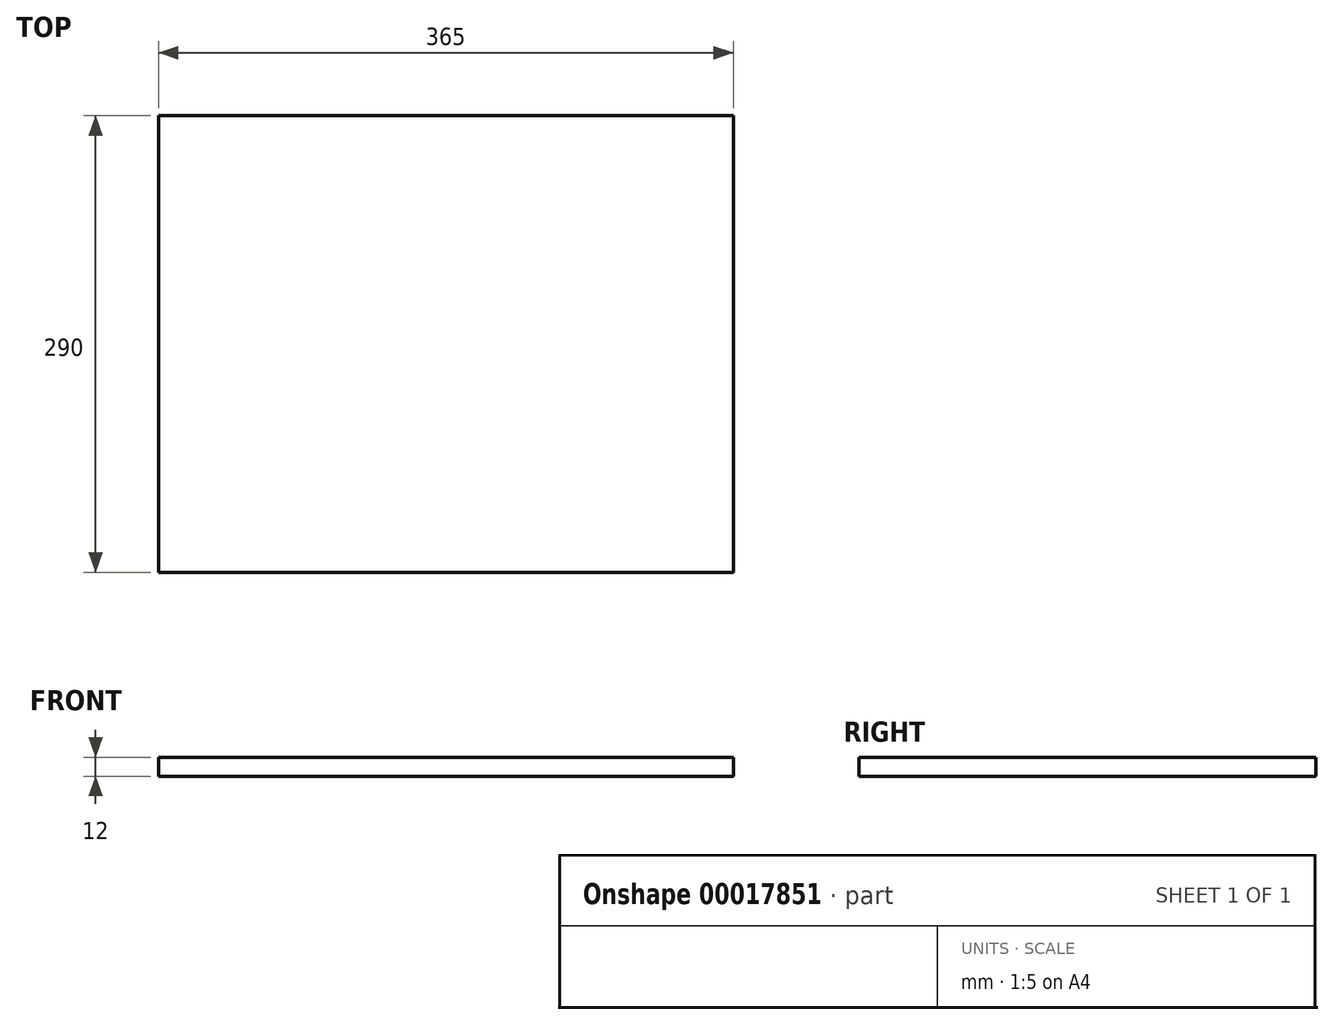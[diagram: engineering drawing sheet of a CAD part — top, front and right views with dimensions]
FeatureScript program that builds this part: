
annotation { "Feature Type Name" : "Feature", "Feature Type Description" : "" }
export const myFeature = defineFeature(function(context is Context, id is Id, definition is map)
    precondition{}
    {
        {
            var Q0;
            Q0=qCreatedBy(makeId("Top.planeOp"),FACE);
            var sketch = newSketch(context, id + "F0", { "sketchPlane" : qUnion([Q0])});
            skLineSegment(sketch, "E0.bottom", {"start": v(-70.96, 65.05) * mm, "end": v(294.04, 65.05) * mm});
            skLineSegment(sketch, "E0.top", {"start": v(-70.96, -224.95) * mm, "end": v(294.04, -224.95) * mm});
            skLineSegment(sketch, "E0.left", {"start": v(-70.96, 65.05) * mm, "end": v(-70.96, -224.95) * mm});
            skLineSegment(sketch, "E0.right", {"start": v(294.04, 65.05) * mm, "end": v(294.04, -224.95) * mm});
            skSolve(sketch);
        }
        {
            var Q0;
            Q0=qSketchRegion(id+"F0",true);
            extrude(context, id + "F1", {"entities" : qUnion([Q0]), "depth" : 12 * mm});
        }
    });
